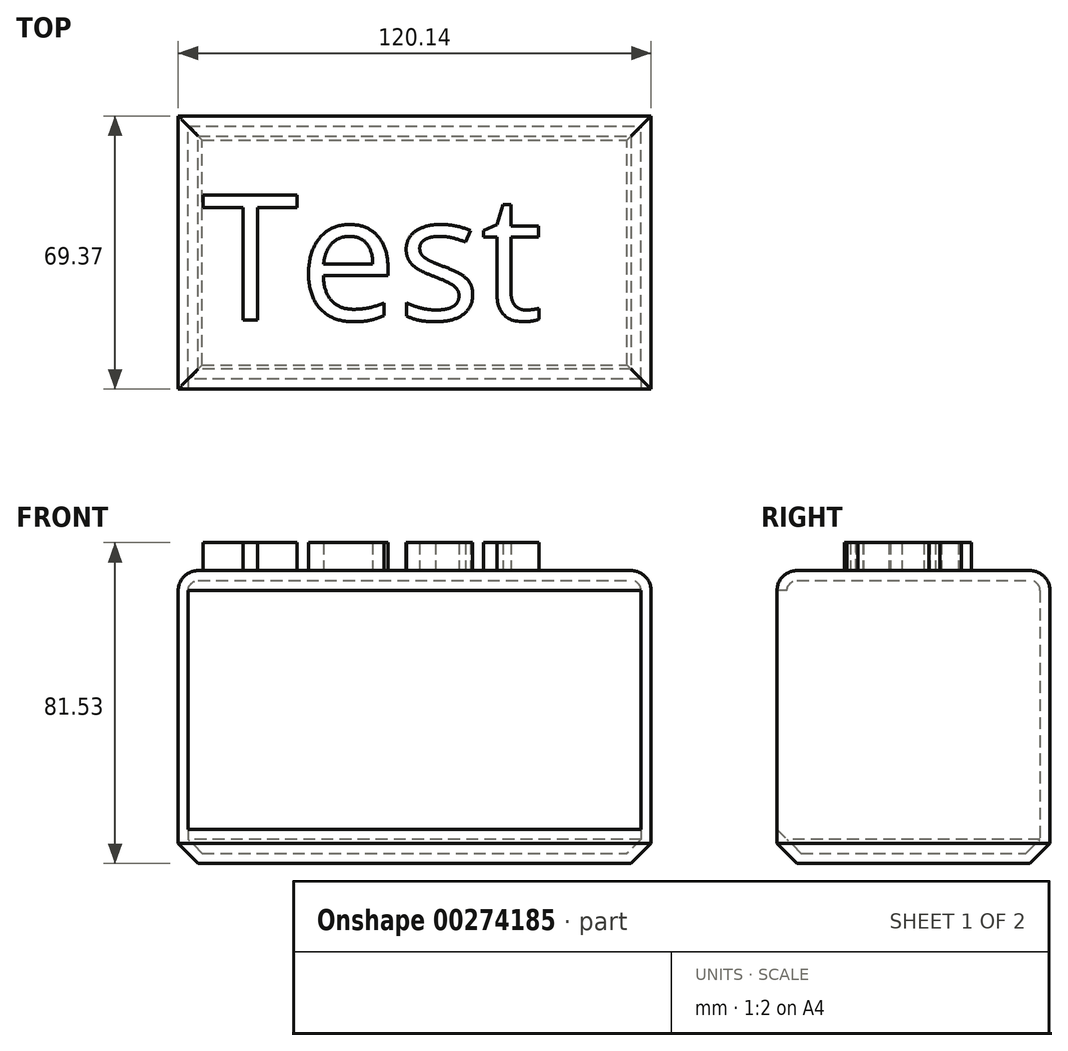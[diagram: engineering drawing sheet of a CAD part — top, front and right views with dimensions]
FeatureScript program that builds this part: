
annotation { "Feature Type Name" : "Feature", "Feature Type Description" : "" }
export const myFeature = defineFeature(function(context is Context, id is Id, definition is map)
    precondition{}
    {
        {
            var Q0;
            Q0=qCreatedBy(makeId("Top.planeOp"),FACE);
            var sketch = newSketch(context, id + "F0", { "sketchPlane" : qUnion([Q0])});
            skLineSegment(sketch, "E0.bottom", {"start": v(0, 0) * mm, "end": v(120.14, 0) * mm});
            skLineSegment(sketch, "E0.top", {"start": v(0, 69.37) * mm, "end": v(120.14, 69.37) * mm});
            skLineSegment(sketch, "E0.left", {"start": v(0, 0) * mm, "end": v(0, 69.37) * mm});
            skLineSegment(sketch, "E0.right", {"start": v(120.14, 0) * mm, "end": v(120.14, 69.37) * mm});
            skSolve(sketch);
        }
        {
            var Q0;
            Q0 = qSketchRegion(id + "F0", true);
            extrude(context, id + "F1", {"entities" : qUnion([Q0]), "depth" : 74.42 * mm});
        }
        {
            var Q0;
            Q0=makeQuery(id+"F1.opExtrude","CAP_FACE",FACE,{"disambiguationData":[OSD([sQuery(id+"F0.wireOp",EDGE,"E0.bottom"),sQuery(id+"F0.wireOp",EDGE,"E0.top"),sQuery(id+"F0.wireOp",EDGE,"E0.left"),sQuery(id+"F0.wireOp",EDGE,"E0.right")])],"isStart":false});
            var sketch = newSketch(context, id + "F2", { "sketchPlane" : qUnion([Q0])});
            skText(sketch, "E1", { "text": "Test ", "fontName": "OpenSans-Regular.ttf"});
            const initialGuessF2  = {"E1": [0.00599, 0.01754, 1, 0, 0.03207]};
            skSetInitialGuess(sketch, initialGuessF2);
            skSolve(sketch);
        }
        {
            var Q0;
            Q0 = qSketchRegion(id + "F2", true);
            extrude(context, id + "F3", {"entities" : qUnion([Q0]), "operationType" : NewBodyOperationType.ADD, "depth" : 7.11 * mm});
        }
        {
            var Q0;
            Q0=makeQuery(id+"F1.opExtrude","CAP_EDGE",EDGE,{"disambiguationData":[OSD([sQuery(id+"F0.wireOp",EDGE,"E0.bottom")])],"isStart":false});
            var Q1;
            Q1=makeQuery(id+"F1.opExtrude","CAP_EDGE",EDGE,{"disambiguationData":[OSD([sQuery(id+"F0.wireOp",EDGE,"E0.left")])],"isStart":false});
            var Q2;
            Q2=makeQuery(id+"F1.opExtrude","CAP_EDGE",EDGE,{"disambiguationData":[OSD([sQuery(id+"F0.wireOp",EDGE,"E0.top")])],"isStart":false});
            var Q3;
            Q3=makeQuery(id+"F1.opExtrude","CAP_EDGE",EDGE,{"disambiguationData":[OSD([sQuery(id+"F0.wireOp",EDGE,"E0.right")])],"isStart":false});
            fillet(context, id + "F4", {"entities" : qUnion([Q0, Q1, Q2, Q3]), "radius" : 5.08 * mm, "tangentPropagation" : true, "allowEdgeOverflow" : false});
        }
        {
            var Q0;
            Q0=makeQuery(id+"F1.opExtrude","CAP_EDGE",EDGE,{"disambiguationData":[OSD([sQuery(id+"F0.wireOp",EDGE,"E0.right")])],"isStart":true});
            var Q1;
            Q1=makeQuery(id+"F1.opExtrude","CAP_EDGE",EDGE,{"disambiguationData":[OSD([sQuery(id+"F0.wireOp",EDGE,"E0.top")])],"isStart":true});
            var Q2;
            Q2=makeQuery(id+"F1.opExtrude","CAP_EDGE",EDGE,{"disambiguationData":[OSD([sQuery(id+"F0.wireOp",EDGE,"E0.left")])],"isStart":true});
            var Q3;
            Q3=makeQuery(id+"F1.opExtrude","CAP_EDGE",EDGE,{"disambiguationData":[OSD([sQuery(id+"F0.wireOp",EDGE,"E0.bottom")])],"isStart":true});
            chamfer(context, id + "F5", {"entities" : qUnion([Q0, Q1, Q2, Q3]), "width" : 5.08 * mm, "tangentPropagation" : true});
        }
        {
            var Q0;
            Q0=makeQuery(id+"F1.opExtrude","SWEPT_FACE",FACE,{"disambiguationData":[OSD([sQuery(id+"F0.wireOp",EDGE,"E0.bottom")])]});
            shell(context, id + "F6", {"entities" : qUnion([Q0]), "thickness" : 2.54 * mm});
        }
    });
